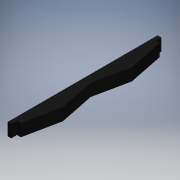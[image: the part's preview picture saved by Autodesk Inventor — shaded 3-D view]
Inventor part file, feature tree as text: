
AUTODESK INVENTOR PART (.ipt)
format: ipt  version: 2017 (Build 210142000, 142)  size: 117,760 bytes
history: native  units: in
note: dims shown in document units (in); Inventor stores cm internally (conversion verified against a paired STEP export)
features: extrude x3, sketch x3
ambient origin geometry x8: Origin, YZ Plane, XZ Plane, XY Plane, X Axis, Y Axis, Z Axis, Center Point
bodies: Solid1 (feature_tree)
feature tree (6):
  extrude  "Extrusion1"  Depth=0.134in
  sketch  "Sketch2"  dims[d2=0.134in d3=0.6115in]
  extrude  "Extrusion2"  Depth=0.134in
  extrude  "Extrusion3"  Depth=0.101in
  sketch  "Sketch1"  dims[d0=2.436in d1=0.134in]
  sketch  "Sketch3"  dims[d4=1.223in d5=0.6115in d6=0.125in d7=0.125in d8=0.2875in d9=0.0in d10=0.065in d11=0.065in d12=0.101in d13=0.0in d14=0.101in d15=0.0in]
